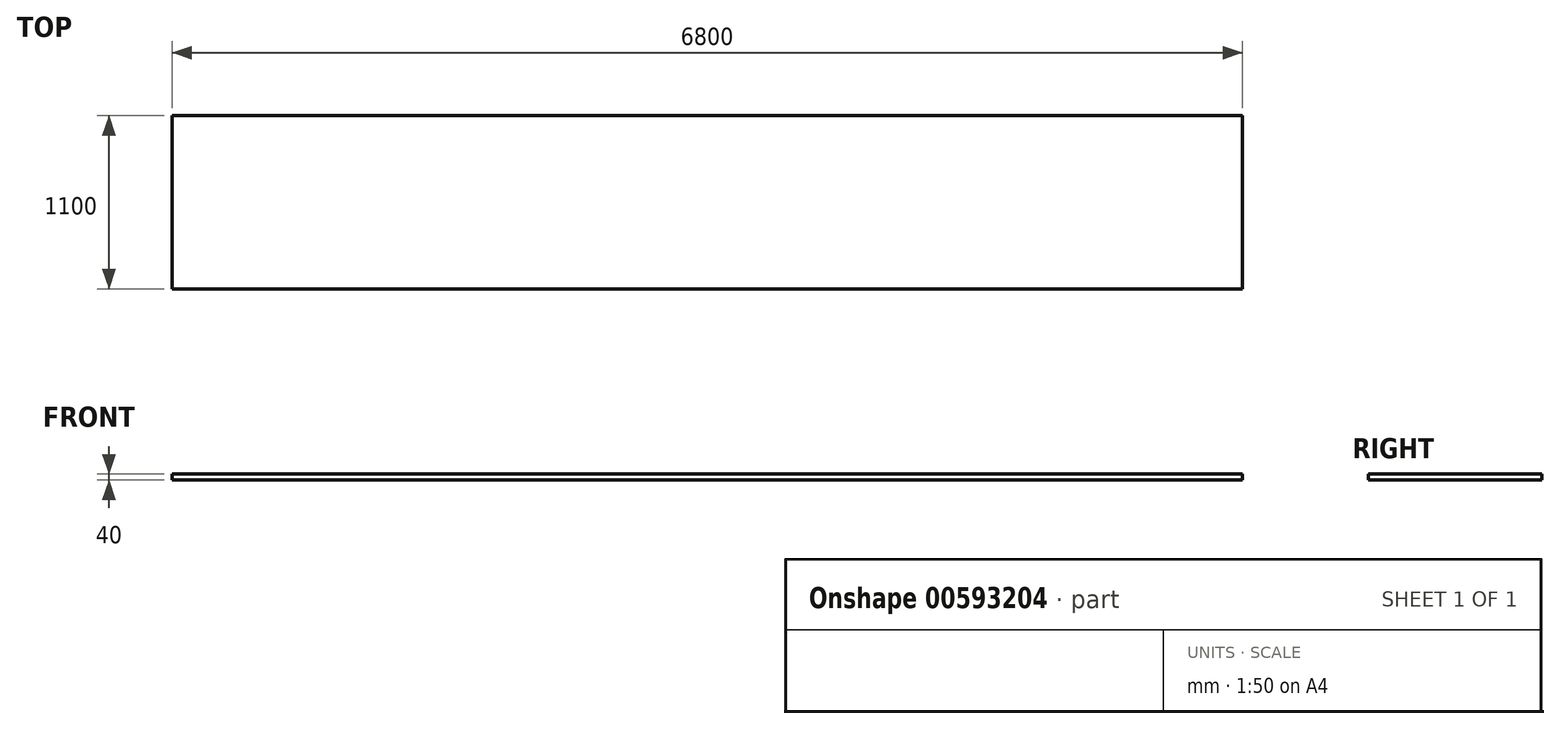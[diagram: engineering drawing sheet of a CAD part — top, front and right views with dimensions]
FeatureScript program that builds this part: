
annotation { "Feature Type Name" : "Feature", "Feature Type Description" : "" }
export const myFeature = defineFeature(function(context is Context, id is Id, definition is map)
    precondition{}
    {
        {
            var Q0;
            Q0=qCreatedBy(makeId("Top.planeOp"),FACE);
            var sketch = newSketch(context, id + "F0", { "sketchPlane" : qUnion([Q0])});
            skLineSegment(sketch, "E0.bottom", {"start": v(0, 0) * mm, "end": v(6800, 0) * mm});
            skLineSegment(sketch, "E0.top", {"start": v(0, 1100) * mm, "end": v(6800, 1100) * mm});
            skLineSegment(sketch, "E0.left", {"start": v(0, 0) * mm, "end": v(0, 1100) * mm});
            skLineSegment(sketch, "E0.right", {"start": v(6800, 0) * mm, "end": v(6800, 1100) * mm});
            skSolve(sketch);
        }
        {
            var Q0;
            Q0=makeQuery(id+"F0.imprint","IMPRINT",FACE,{"disambiguationData":[TD([[makeQuery(id+"F0.imprint","IMPRINT",EDGE,{"derivedFrom":sQuery(id+"F0.wireOp",EDGE,"E0.bottom")}),1.0]])]});
            extrude(context, id + "F1", {"entities" : qUnion([Q0]), "depth" : 40 * mm, "offsetDistance" : 25 * mm});
        }
    });
